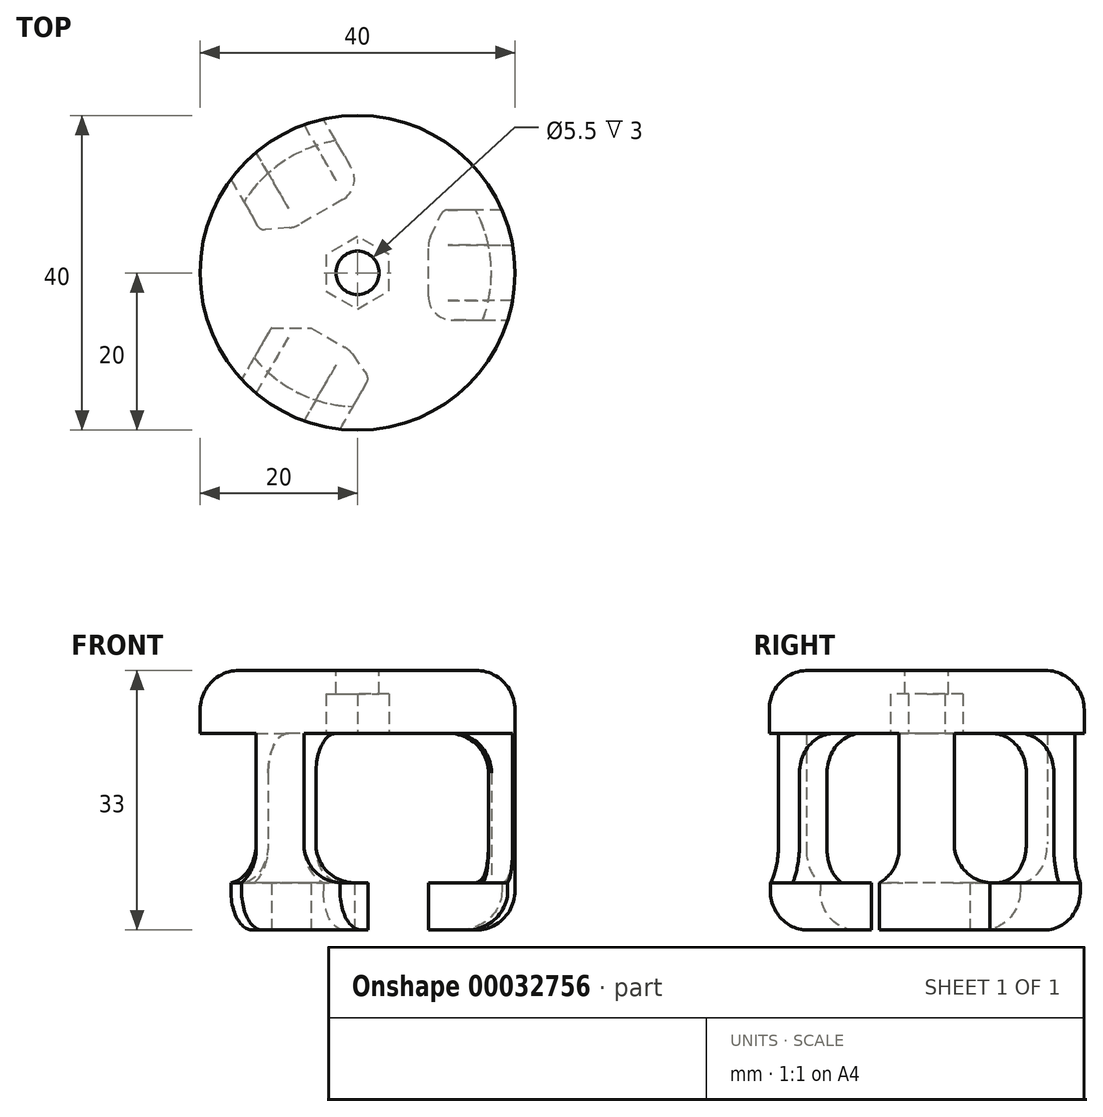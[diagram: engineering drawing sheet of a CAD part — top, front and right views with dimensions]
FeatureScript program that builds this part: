
annotation { "Feature Type Name" : "Feature", "Feature Type Description" : "" }
export const myFeature = defineFeature(function(context is Context, id is Id, definition is map)
    precondition{}
    {
        {
            var Q0;
            Q0=qCreatedBy(makeId("Front.planeOp"),FACE);
            var sketch = newSketch(context, id + "F0", { "sketchPlane" : qUnion([Q0])});
            skLineSegment(sketch, "E0", {"start": v(0, 0) * mm, "end": v(20, 0) * mm});
            skLineSegment(sketch, "E1", {"start": v(20, -33) * mm, "end": v(10, -33) * mm});
            skLineSegment(sketch, "E2", {"start": v(10, -33) * mm, "end": v(10, -28) * mm});
            skLineSegment(sketch, "E3", {"start": v(10, -28) * mm, "end": v(17, -28) * mm});
            skLineSegment(sketch, "E4", {"start": v(0, -8) * mm, "end": v(0, 0) * mm});
            skLineSegment(sketch, "E5", {"start": v(0, 0) * mm, "end": v(0, 12.35) * mm, "construction": true});
            skLineSegment(sketch, "E6", {"start": v(20, 0) * mm, "end": v(20, -33) * mm});
            skLineSegment(sketch, "E7", {"start": v(0, -8) * mm, "end": v(17, -8) * mm});
            skLineSegment(sketch, "E8", {"start": v(17, -8) * mm, "end": v(17, -28) * mm});
            skSolve(sketch);
        }
        {
            var Q0;
            Q0 = qSketchRegion(id + "F0", true);
            var Q1;
            Q1=sQuery(id+"F0.wireOp",EDGE,"E5");
            revolve(context, id + "F1", {"entities" : qUnion([Q0]), "axis" : qUnion([Q1]), "revolveType" : RevolveType.FULL});
        }
        {
            var Q0;
            Q0=makeQuery(id+"F1.opRevolve","SWEPT_FACE",FACE,{"disambiguationData":[OSD([sQuery(id+"F0.wireOp",EDGE,"E1")])]});
            var sketch = newSketch(context, id + "F2", { "sketchPlane" : qUnion([Q0])});
            skLineSegment(sketch, "E9.bottom", {"start": v(7, 0) * mm, "end": v(22.64, 0) * mm});
            skLineSegment(sketch, "E9.top", {"start": v(7, 3) * mm, "end": v(22.64, 3) * mm});
            skLineSegment(sketch, "E9.left", {"start": v(7, 0) * mm, "end": v(7, 3) * mm});
            skLineSegment(sketch, "E9.right", {"start": v(22.64, 0) * mm, "end": v(22.64, 3) * mm});
            skPoint(sketch, "E10", {"position": v(7, 1.5) * mm});
            skLineSegment(sketch, "E11.1.0", {"start": v(-3.5, 6.06) * mm, "end": v(-6.1, 4.56) * mm});
            skLineSegment(sketch, "E11.1.1", {"start": v(-3.5, 6.06) * mm, "end": v(-11.32, 19.6) * mm});
            skLineSegment(sketch, "E11.1.2", {"start": v(-6.1, 4.56) * mm, "end": v(-13.92, 18.1) * mm});
            skLineSegment(sketch, "E11.1.3", {"start": v(-11.32, 19.6) * mm, "end": v(-13.92, 18.1) * mm});
            skPoint(sketch, "E11.1.4", {"position": v(-4.8, 5.31) * mm});
            skLineSegment(sketch, "E11.2.0", {"start": v(-3.5, -6.06) * mm, "end": v(-0.9, -7.56) * mm});
            skLineSegment(sketch, "E11.2.1", {"start": v(-3.5, -6.06) * mm, "end": v(-11.32, -19.6) * mm});
            skLineSegment(sketch, "E11.2.2", {"start": v(-0.9, -7.56) * mm, "end": v(-8.72, -21.1) * mm});
            skLineSegment(sketch, "E11.2.3", {"start": v(-11.32, -19.6) * mm, "end": v(-8.72, -21.1) * mm});
            skPoint(sketch, "E11.2.4", {"position": v(-2.2, -6.81) * mm});
            skPoint(sketch, "E11.center", {"position": v(0, 0) * mm});
            skCircle(sketch, "E12", {"center": v(0, 0) * mm, "radius": 27.07 * mm});
            skSolve(sketch);
        }
        {
            var Q0;
            Q0 = qSketchRegion(id + "F2", true);
            var Q1;
            Q1=makeQuery(id+"F1.opRevolve","SWEPT_FACE",FACE,{"disambiguationData":[OSD([sQuery(id+"F0.wireOp",EDGE,"507b1540-1300-4f00-8e0e-256bcd7e9e75")])]});
            extrude(context, id + "F3", {"entities" : qUnion([Q0]), "operationType" : NewBodyOperationType.REMOVE, "oppositeDirection" : true, "endBoundEntityFace" : qUnion([Q1]), "depth" : 6 * mm});
        }
        {
            var Q0;
            Q0=makeQuery(id+"F1.opRevolve","SWEPT_FACE",FACE,{"disambiguationData":[OSD([sQuery(id+"F0.wireOp",EDGE,"E1")])]});
            var sketch = newSketch(context, id + "F4", { "sketchPlane" : qUnion([Q0])});
            skLineSegment(sketch, "E13", {"start": v(9.28, -4.6) * mm, "end": v(10.6, -7.42) * mm});
            skLineSegment(sketch, "E14", {"start": v(19.08, 6) * mm, "end": v(12, 6) * mm});
            skPoint(sketch, "E15.visualSharp", {"position": v(8.5, 6) * mm});
            skArc(sketch, "E15.filletArc", {"start": v(12, 6) * mm, "mid": v(9.88, 5.12) * mm, "end": v(9, 3) * mm});
            skArc(sketch, "E16.filletArc", {"start": v(10.6, -7.42) * mm, "mid": v(10.97, -7.84) * mm, "end": v(11.5, -8) * mm});
            skArc(sketch, "E17", {"start": v(18.33, -8) * mm, "mid": v(19.97, -1.07) * mm, "end": v(19.08, 6) * mm});
            skLineSegment(sketch, "E18", {"start": v(11.5, -8) * mm, "end": v(18.33, -8) * mm});
            skLineSegment(sketch, "E19", {"start": v(9, 3) * mm, "end": v(9, -3.33) * mm});
            skPoint(sketch, "E20.visualSharp", {"position": v(9, -4) * mm});
            skArc(sketch, "E20.filletArc", {"start": v(9, -3.33) * mm, "mid": v(9.07, -3.98) * mm, "end": v(9.28, -4.6) * mm});
            skLineSegment(sketch, "E21.1.0", {"start": v(-14.74, 13.52) * mm, "end": v(-11.2, 7.4) * mm});
            skPoint(sketch, "E21.1.1", {"position": v(-1.04, 9.8) * mm});
            skPoint(sketch, "E21.1.2", {"position": v(-9.45, 4.36) * mm});
            skArc(sketch, "E21.1.3", {"start": v(-11.2, 7.4) * mm, "mid": v(-9.37, 6) * mm, "end": v(-7.1, 6.3) * mm});
            skLineSegment(sketch, "E21.1.4", {"start": v(-0.65, 10.34) * mm, "end": v(1.13, 12.89) * mm});
            skLineSegment(sketch, "E21.1.5", {"start": v(-7.1, 6.3) * mm, "end": v(-1.61, 9.46) * mm});
            skLineSegment(sketch, "E21.1.6", {"start": v(1.18, 13.96) * mm, "end": v(-2.24, 19.87) * mm});
            skArc(sketch, "E21.1.7", {"start": v(-2.24, 19.87) * mm, "mid": v(-9.06, 17.83) * mm, "end": v(-14.74, 13.52) * mm});
            skArc(sketch, "E21.1.8", {"start": v(1.13, 12.89) * mm, "mid": v(1.31, 13.42) * mm, "end": v(1.18, 13.96) * mm});
            skArc(sketch, "E21.1.9", {"start": v(-1.61, 9.46) * mm, "mid": v(-1.09, 9.85) * mm, "end": v(-0.65, 10.34) * mm});
            skLineSegment(sketch, "E21.2.0", {"start": v(-4.34, -19.52) * mm, "end": v(-0.8, -13.4) * mm});
            skPoint(sketch, "E21.2.1", {"position": v(-7.96, -5.8) * mm});
            skPoint(sketch, "E21.2.2", {"position": v(0.95, -10.36) * mm});
            skArc(sketch, "E21.2.3", {"start": v(-0.8, -13.4) * mm, "mid": v(-0.5, -11.12) * mm, "end": v(-1.9, -9.3) * mm});
            skLineSegment(sketch, "E21.2.4", {"start": v(-8.63, -5.74) * mm, "end": v(-11.73, -5.47) * mm});
            skLineSegment(sketch, "E21.2.5", {"start": v(-1.9, -9.3) * mm, "end": v(-7.39, -6.13) * mm});
            skLineSegment(sketch, "E21.2.6", {"start": v(-12.68, -5.96) * mm, "end": v(-16.1, -11.87) * mm});
            skArc(sketch, "E21.2.7", {"start": v(-16.1, -11.87) * mm, "mid": v(-10.91, -16.76) * mm, "end": v(-4.34, -19.52) * mm});
            skArc(sketch, "E21.2.8", {"start": v(-11.73, -5.47) * mm, "mid": v(-12.28, -5.57) * mm, "end": v(-12.68, -5.96) * mm});
            skArc(sketch, "E21.2.9", {"start": v(-7.39, -6.13) * mm, "mid": v(-7.99, -5.86) * mm, "end": v(-8.63, -5.74) * mm});
            skSolve(sketch);
        }
        {
            var Q0;
            Q0 = qSketchRegion(id + "F4", true);
            var Q1;
            Q1=makeQuery(id+"F3.boolean.opBoolean","COPY",FACE,{"disambiguationData":[OD(0.0)],"derivedFrom":makeQuery(id+"F3.opExtrude","CAP_FACE",FACE,{"disambiguationData":[OSD([sQuery(id+"F2.wireOp",EDGE,"E9.bottom"),sQuery(id+"F2.wireOp",EDGE,"E9.top"),sQuery(id+"F2.wireOp",EDGE,"E9.left"),sQuery(id+"F2.wireOp",EDGE,"E9.right"),sQuery(id+"F2.wireOp",EDGE,"E11.1.0"),sQuery(id+"F2.wireOp",EDGE,"E11.1.1"),sQuery(id+"F2.wireOp",EDGE,"E11.1.2"),sQuery(id+"F2.wireOp",EDGE,"E11.1.3"),sQuery(id+"F2.wireOp",EDGE,"E11.2.0"),sQuery(id+"F2.wireOp",EDGE,"E11.2.1"),sQuery(id+"F2.wireOp",EDGE,"E11.2.2"),sQuery(id+"F2.wireOp",EDGE,"E11.2.3"),sQuery(id+"F2.wireOp",EDGE,"E12")])],"isStart":false})});
            extrude(context, id + "F5", {"entities" : qUnion([Q0]), "operationType" : NewBodyOperationType.ADD, "endBound" : BoundingType.UP_TO_SURFACE, "oppositeDirection" : true, "endBoundEntityFace" : qUnion([Q1]), "depth" : 25 * mm});
        }
        {
            var Q0;
            Q0=makeQuery(id+"F3.boolean.opBoolean","COPY",FACE,{"disambiguationData":[OD(0.0)],"derivedFrom":makeQuery(id+"F3.opExtrude","CAP_FACE",FACE,{"disambiguationData":[OSD([sQuery(id+"F2.wireOp",EDGE,"E9.bottom"),sQuery(id+"F2.wireOp",EDGE,"E9.top"),sQuery(id+"F2.wireOp",EDGE,"E9.left"),sQuery(id+"F2.wireOp",EDGE,"E9.right"),sQuery(id+"F2.wireOp",EDGE,"E11.1.0"),sQuery(id+"F2.wireOp",EDGE,"E11.1.1"),sQuery(id+"F2.wireOp",EDGE,"E11.1.2"),sQuery(id+"F2.wireOp",EDGE,"E11.1.3"),sQuery(id+"F2.wireOp",EDGE,"E11.2.0"),sQuery(id+"F2.wireOp",EDGE,"E11.2.1"),sQuery(id+"F2.wireOp",EDGE,"E11.2.2"),sQuery(id+"F2.wireOp",EDGE,"E11.2.3"),sQuery(id+"F2.wireOp",EDGE,"E12")])],"isStart":false})});
            var sketch = newSketch(context, id + "F6", { "sketchPlane" : qUnion([Q0])});
            skArc(sketch, "E22", {"start": v(16.64, -3.5) * mm, "mid": v(17, 0) * mm, "end": v(16.64, 3.5) * mm, "construction": true});
            skArc(sketch, "E23", {"start": v(21.66, -3.5) * mm, "mid": v(21.94, 0) * mm, "end": v(21.66, 3.5) * mm, "construction": true});
            skLineSegment(sketch, "E24", {"start": v(16.64, 3.5) * mm, "end": v(21.66, 3.5) * mm});
            skLineSegment(sketch, "E25", {"start": v(21.66, -3.5) * mm, "end": v(16.64, -3.5) * mm});
            skArc(sketch, "E26.1.0", {"start": v(-5.29, 16.16) * mm, "mid": v(-8.5, 14.72) * mm, "end": v(-11.35, 12.66) * mm, "construction": true});
            skArc(sketch, "E26.1.1", {"start": v(-7.8, 20.5) * mm, "mid": v(-10.97, 19) * mm, "end": v(-13.86, 17) * mm, "construction": true});
            skLineSegment(sketch, "E26.1.2", {"start": v(-7.8, 20.5) * mm, "end": v(-5.29, 16.16) * mm});
            skLineSegment(sketch, "E26.1.3", {"start": v(-11.35, 12.66) * mm, "end": v(-13.86, 17) * mm});
            skArc(sketch, "E26.2.0", {"start": v(-11.35, -12.66) * mm, "mid": v(-8.5, -14.72) * mm, "end": v(-5.29, -16.16) * mm, "construction": true});
            skArc(sketch, "E26.2.1", {"start": v(-13.86, -17) * mm, "mid": v(-10.97, -19) * mm, "end": v(-7.8, -20.5) * mm, "construction": true});
            skLineSegment(sketch, "E26.2.2", {"start": v(-13.86, -17) * mm, "end": v(-11.35, -12.66) * mm});
            skLineSegment(sketch, "E26.2.3", {"start": v(-5.29, -16.16) * mm, "end": v(-7.8, -20.5) * mm});
            skArc(sketch, "E27", {"start": v(16.64, 3.5) * mm, "mid": v(8.5, 14.72) * mm, "end": v(-5.29, 16.16) * mm});
            skArc(sketch, "E28", {"start": v(-11.35, 12.66) * mm, "mid": v(-17, 0) * mm, "end": v(-11.35, -12.66) * mm});
            skArc(sketch, "E29", {"start": v(-5.29, -16.16) * mm, "mid": v(8.5, -14.72) * mm, "end": v(16.64, -3.5) * mm});
            skArc(sketch, "E30", {"start": v(21.66, 3.5) * mm, "mid": v(10.97, 19) * mm, "end": v(-7.8, 20.5) * mm});
            skArc(sketch, "E31", {"start": v(-13.86, 17) * mm, "mid": v(-21.94, 0) * mm, "end": v(-13.86, -17) * mm});
            skArc(sketch, "E32", {"start": v(-7.8, -20.5) * mm, "mid": v(10.97, -19) * mm, "end": v(21.66, -3.5) * mm});
            skSolve(sketch);
        }
        {
            var Q0;
            Q0 = qSketchRegion(id + "F6", true);
            var Q1;
            Q1=makeQuery(id+"F1.opRevolve","SWEPT_FACE",FACE,{"disambiguationData":[OSD([sQuery(id+"F0.wireOp",EDGE,"E7")])]});
            extrude(context, id + "F7", {"entities" : qUnion([Q0]), "operationType" : NewBodyOperationType.REMOVE, "endBound" : BoundingType.UP_TO_SURFACE, "oppositeDirection" : true, "endBoundEntityFace" : qUnion([Q1]), "depth" : 18 * mm});
        }
        {
            var Q0;
            Q0=makeQuery(id+"FRc7LSiDmBRHnpg_1.opFillet","SPLIT",FACE,{"disambiguationData":[OD(0.0)],"derivedFrom":makeQuery(id+"F1.opRevolve","SWEPT_FACE",FACE,{"disambiguationData":[OSD([sQuery(id+"F0.wireOp",EDGE,"E0")])]})});
            var sketch = newSketch(context, id + "F8", { "sketchPlane" : qUnion([Q0])});
            skLineSegment(sketch, "E33", {"start": v(12.7, 22) * mm, "end": v(0, 0) * mm});
            skPoint(sketch, "E34.endSnap0", {"position": v(-6, 0) * mm});
            skLineSegment(sketch, "E35", {"start": v(0, 0) * mm, "end": v(26.35, 0) * mm});
            skSolve(sketch);
        }
        {
            var Q0;
            Q0=makeQuery(id+"F7.boolean.opBoolean","COPY",EDGE,{"derivedFrom":makeQuery(id+"F7.opExtrude","CAP_EDGE",EDGE,{"disambiguationData":[OSD([sQuery(id+"F6.wireOp",EDGE,"E25")])],"isStart":true})});
            var Q1;
            Q1=makeQuery(id+"F7.boolean.opBoolean","COPY",EDGE,{"derivedFrom":makeQuery(id+"F7.opExtrude","CAP_EDGE",EDGE,{"disambiguationData":[OSD([sQuery(id+"F6.wireOp",EDGE,"E24")])],"isStart":true})});
            var Q2;
            Q2=makeQuery(id+"F7.boolean.opBoolean","COPY",EDGE,{"derivedFrom":makeQuery(id+"F7.opExtrude","CAP_EDGE",EDGE,{"disambiguationData":[OSD([sQuery(id+"F6.wireOp",EDGE,"E26.2.3")])],"isStart":true})});
            var Q3;
            Q3=makeQuery(id+"F7.boolean.opBoolean","COPY",EDGE,{"derivedFrom":makeQuery(id+"F7.opExtrude","CAP_EDGE",EDGE,{"disambiguationData":[OSD([sQuery(id+"F6.wireOp",EDGE,"E26.2.2")])],"isStart":true})});
            var Q4;
            Q4=makeQuery(id+"F7.boolean.opBoolean","COPY",EDGE,{"derivedFrom":makeQuery(id+"F7.opExtrude","CAP_EDGE",EDGE,{"disambiguationData":[OSD([sQuery(id+"F6.wireOp",EDGE,"E26.1.3")])],"isStart":true})});
            var Q5;
            Q5=makeQuery(id+"F7.boolean.opBoolean","COPY",EDGE,{"derivedFrom":makeQuery(id+"F7.opExtrude","CAP_EDGE",EDGE,{"disambiguationData":[OSD([sQuery(id+"F6.wireOp",EDGE,"E26.1.2")])],"isStart":true})});
            fillet(context, id + "F9", {"entities" : qUnion([Q0, Q1, Q2, Q3, Q4, Q5]), "radius" : 5 * mm, "tangentPropagation" : true, "allowEdgeOverflow" : false});
        }
        {
            var Q0;
            {var subQ0=sQuery(id+"F0.wireOp",EDGE,"5JU0XVHw-jdRx-ohpi-ptgh-7lzUt1P3IJOZ");var subQ1=sQuery(id+"F0.wireOp",EDGE,"AD1YDz8e-BfkL-U70Y-Slmf-86ug7eZmjnSb");Q0=makeQuery(id+"F7.boolean.opBoolean","SPLIT",EDGE,{"disambiguationData":[TD([makeQuery(id+"F7.opExtrude","SWEPT_FACE",FACE,{"disambiguationData":[OSD([sQuery(id+"F6.wireOp",EDGE,"E26.2.2")])]})])],"derivedFrom":makeQuery(id+"F1.opRevolve","SWEPT_EDGE",EDGE,{"disambiguationData":[OSD([subQ1,subQ0])]})});}
            var Q1;
            {var subQ0=sQuery(id+"F0.wireOp",EDGE,"5JU0XVHw-jdRx-ohpi-ptgh-7lzUt1P3IJOZ");var subQ1=sQuery(id+"F0.wireOp",EDGE,"AD1YDz8e-BfkL-U70Y-Slmf-86ug7eZmjnSb");Q1=makeQuery(id+"F7.boolean.opBoolean","SPLIT",EDGE,{"disambiguationData":[TD([makeQuery(id+"F7.opExtrude","SWEPT_FACE",FACE,{"disambiguationData":[OSD([sQuery(id+"F6.wireOp",EDGE,"E26.1.2")])]})])],"derivedFrom":makeQuery(id+"F1.opRevolve","SWEPT_EDGE",EDGE,{"disambiguationData":[OSD([subQ1,subQ0])]})});}
            var Q2;
            {var subQ0=sQuery(id+"F0.wireOp",EDGE,"5JU0XVHw-jdRx-ohpi-ptgh-7lzUt1P3IJOZ");var subQ1=sQuery(id+"F0.wireOp",EDGE,"AD1YDz8e-BfkL-U70Y-Slmf-86ug7eZmjnSb");Q2=makeQuery(id+"F7.boolean.opBoolean","SPLIT",EDGE,{"disambiguationData":[TD([makeQuery(id+"F7.opExtrude","SWEPT_FACE",FACE,{"disambiguationData":[OSD([sQuery(id+"F6.wireOp",EDGE,"E24")])]})])],"derivedFrom":makeQuery(id+"F1.opRevolve","SWEPT_EDGE",EDGE,{"disambiguationData":[OSD([subQ1,subQ0])]})});}
            var Q3;
            {var subQ0=sQuery(id+"F0.wireOp",EDGE,"E6");var subQ1=sQuery(id+"F0.wireOp",EDGE,"YB5l314j-i3Ki-3XtK-FZlX-X9e5m8dVZ1rk");Q3=makeQuery(id+"F7.boolean.opBoolean","SPLIT",EDGE,{"disambiguationData":[TD([makeQuery(id+"F7.opExtrude","SWEPT_FACE",FACE,{"disambiguationData":[OSD([sQuery(id+"F6.wireOp",EDGE,"E24")])]})])],"derivedFrom":makeQuery(id+"F1.opRevolve","SWEPT_EDGE",EDGE,{"disambiguationData":[OSD([subQ0,subQ1])]})});}
            var Q4;
            {var subQ0=sQuery(id+"F0.wireOp",EDGE,"E6");var subQ1=sQuery(id+"F0.wireOp",EDGE,"YB5l314j-i3Ki-3XtK-FZlX-X9e5m8dVZ1rk");Q4=makeQuery(id+"F7.boolean.opBoolean","SPLIT",EDGE,{"disambiguationData":[TD([makeQuery(id+"F7.opExtrude","SWEPT_FACE",FACE,{"disambiguationData":[OSD([sQuery(id+"F6.wireOp",EDGE,"E26.2.2")])]})])],"derivedFrom":makeQuery(id+"F1.opRevolve","SWEPT_EDGE",EDGE,{"disambiguationData":[OSD([subQ0,subQ1])]})});}
            var Q5;
            {var subQ0=sQuery(id+"F0.wireOp",EDGE,"E6");var subQ1=sQuery(id+"F0.wireOp",EDGE,"YB5l314j-i3Ki-3XtK-FZlX-X9e5m8dVZ1rk");Q5=makeQuery(id+"F7.boolean.opBoolean","SPLIT",EDGE,{"disambiguationData":[TD([makeQuery(id+"F7.opExtrude","SWEPT_FACE",FACE,{"disambiguationData":[OSD([sQuery(id+"F6.wireOp",EDGE,"E26.1.2")])]})])],"derivedFrom":makeQuery(id+"F1.opRevolve","SWEPT_EDGE",EDGE,{"disambiguationData":[OSD([subQ0,subQ1])]})});}
            fillet(context, id + "F10", {"entities" : qUnion([Q0, Q1, Q2, Q3, Q4, Q5]), "radius" : 5 * mm, "tangentPropagation" : true, "allowEdgeOverflow" : false});
        }
        {
            var Q0;
            {var subQ0=sQuery(id+"F0.wireOp",EDGE,"E7");Q0=makeQuery(id+"F7.boolean.opBoolean","MERGE",FACE,{"derivedFrom":[makeQuery(id+"F1.opRevolve","SWEPT_FACE",FACE,{"disambiguationData":[OSD([subQ0])]}),makeQuery(id+"F7.opExtrude","CAP_FACE",FACE,{"disambiguationData":[OSD([subQ0]),ownerDisambiguation([makeQuery(id+"F7.opExtrude","SWEPT_BODY",BODY,{"disambiguationData":[OSD([sQuery(id+"F6.wireOp",EDGE,"E24"),sQuery(id+"F6.wireOp",EDGE,"E26.1.2"),sQuery(id+"F6.wireOp",EDGE,"E27"),sQuery(id+"F6.wireOp",EDGE,"E30")])]})])],"isStart":false}),makeQuery(id+"F7.opExtrude","CAP_FACE",FACE,{"disambiguationData":[OSD([subQ0]),ownerDisambiguation([makeQuery(id+"F7.opExtrude","SWEPT_BODY",BODY,{"disambiguationData":[OSD([sQuery(id+"F6.wireOp",EDGE,"E25"),sQuery(id+"F6.wireOp",EDGE,"E26.2.3"),sQuery(id+"F6.wireOp",EDGE,"E29"),sQuery(id+"F6.wireOp",EDGE,"E32")])]})])],"isStart":false}),makeQuery(id+"F7.opExtrude","CAP_FACE",FACE,{"disambiguationData":[OSD([subQ0]),ownerDisambiguation([makeQuery(id+"F7.opExtrude","SWEPT_BODY",BODY,{"disambiguationData":[OSD([sQuery(id+"F6.wireOp",EDGE,"E26.1.3"),sQuery(id+"F6.wireOp",EDGE,"E26.2.2"),sQuery(id+"F6.wireOp",EDGE,"E28"),sQuery(id+"F6.wireOp",EDGE,"E31")])]})])],"isStart":false})]});}
            var sketch = newSketch(context, id + "F11", { "sketchPlane" : qUnion([Q0])});
            skCircle(sketch, "E36.cCircle", {"center": v(0, 0) * mm, "radius": 4 * mm, "construction": true});
            skLineSegment(sketch, "E36.0", {"start": v(-4, 2.3) * mm, "end": v(0, 4.62) * mm});
            skLineSegment(sketch, "E36.1", {"start": v(0, 4.62) * mm, "end": v(4, 2.3) * mm});
            skLineSegment(sketch, "E36.2", {"start": v(4, 2.3) * mm, "end": v(4, -2.3) * mm});
            skLineSegment(sketch, "E36.3", {"start": v(4, -2.3) * mm, "end": v(0, -4.62) * mm});
            skLineSegment(sketch, "E36.4", {"start": v(0, -4.62) * mm, "end": v(-4, -2.3) * mm});
            skLineSegment(sketch, "E36.5", {"start": v(-4, -2.3) * mm, "end": v(-4, 2.3) * mm});
            skPoint(sketch, "E36.0.midPoint", {"position": v(-2, 3.46) * mm});
            skSolve(sketch);
        }
        {
            var Q0;
            Q0 = qSketchRegion(id + "F11", true);
            extrude(context, id + "F12", {"entities" : qUnion([Q0]), "operationType" : NewBodyOperationType.REMOVE, "oppositeDirection" : true, "depth" : 5 * mm});
        }
        {
            var Q0;
            Q0=sQuery(id+"F8.wireOp",VERTEX,"E35.start");
            var Q1;
            Q1=makeQuery(id+"F1.opRevolve","SWEPT_BODY",BODY,{"disambiguationData":[OSD([sQuery(id+"F0.wireOp",EDGE,"E0"),sQuery(id+"F0.wireOp",EDGE,"E1"),sQuery(id+"F0.wireOp",EDGE,"E2"),sQuery(id+"F0.wireOp",EDGE,"E3"),sQuery(id+"F0.wireOp",EDGE,"E4"),sQuery(id+"F0.wireOp",EDGE,"E6"),sQuery(id+"F0.wireOp",EDGE,"E7"),sQuery(id+"F0.wireOp",EDGE,"oZZgMhXo-IGQ9-ketN-pIXG-lvkoXyTYYKlg"),sQuery(id+"F0.wireOp",EDGE,"dHxaSU61-WMZi-X72z-Avvv-rAPENNYPcqco"),sQuery(id+"F0.wireOp",EDGE,"AD1YDz8e-BfkL-U70Y-Slmf-86ug7eZmjnSb"),sQuery(id+"F0.wireOp",EDGE,"5JU0XVHw-jdRx-ohpi-ptgh-7lzUt1P3IJOZ")])]});
            hole(context, id + "F13", {"style" : HoleStyle.SIMPLE, "endStyle" : HoleEndStyle.THROUGH, "holeDiameter" : 5.5 * mm, "locations" : qUnion([Q0]), "scope" : qUnion([Q1]), "isTappedThrough" : true});
        }
        {
            var Q0;
            Q0=qCreatedBy(makeId("Front.planeOp"),FACE);
            var sketch = newSketch(context, id + "F14", { "sketchPlane" : qUnion([Q0])});
            skLineSegment(sketch, "E37.bottom", {"start": v(-23.38, -22.81) * mm, "end": v(4.84, -22.81) * mm});
            skLineSegment(sketch, "E37.top", {"start": v(-23.38, -36.77) * mm, "end": v(4.84, -36.77) * mm});
            skLineSegment(sketch, "E37.left", {"start": v(-23.38, -22.81) * mm, "end": v(-23.38, -36.77) * mm});
            skLineSegment(sketch, "E37.right", {"start": v(4.84, -22.81) * mm, "end": v(4.84, -36.77) * mm});
            skSolve(sketch);
        }
        {
            var Q0;
            Q0 = qSketchRegion(id + "F14", true);
            extrude(context, id + "F15", {"entities" : qUnion([Q0]), "operationType" : NewBodyOperationType.REMOVE, "depth" : 7 * mm});
        }
        {
            var Q0;
            Q0=qCreatedBy(makeId("Front.planeOp"),FACE);
            cPlane(context, id + "F16", {"entities" : qUnion([Q0]), "cplaneType" : CPlaneType.OFFSET, "offset" : 25 * mm, "oppositeDirection" : true, "width" : 150 * mm, "height" : 150 * mm});
        }
        {
            var Q0;
            {var subQ0=sQuery(id+"F6.wireOp",EDGE,"E24");var subQ1=sQuery(id+"F0.wireOp",EDGE,"E8");var subQ3=sQuery(id+"F0.wireOp",EDGE,"E7");Q0=makeQuery(id+"F7.boolean.opBoolean","SPLIT",EDGE,{"disambiguationData":[TD([makeQuery(id+"F7.opExtrude","SWEPT_FACE",FACE,{"disambiguationData":[OSD([subQ0])]})])],"derivedFrom":makeQuery(id+"F1.opRevolve","SWEPT_EDGE",EDGE,{"disambiguationData":[OSD([subQ3,subQ1])]})});}
            var Q1;
            Q1=makeQuery(id+"F7.boolean.opBoolean","COPY",EDGE,{"derivedFrom":makeQuery(id+"F7.opExtrude","TWEAK_EDGE",EDGE,{"derivedFrom":[makeQuery(id+"F1.opRevolve","SWEPT_FACE",FACE,{"disambiguationData":[OSD([sQuery(id+"F0.wireOp",EDGE,"E7")])]}),makeQuery(id+"F6.imprint","IMPRINT",EDGE,{"derivedFrom":sQuery(id+"F6.wireOp",EDGE,"E25")})]})});
            var Q2;
            Q2=makeQuery(id+"F7.boolean.opBoolean","COPY",EDGE,{"derivedFrom":makeQuery(id+"F7.opExtrude","TWEAK_EDGE",EDGE,{"derivedFrom":[makeQuery(id+"F1.opRevolve","SWEPT_FACE",FACE,{"disambiguationData":[OSD([sQuery(id+"F0.wireOp",EDGE,"E7")])]}),makeQuery(id+"F6.imprint","IMPRINT",EDGE,{"derivedFrom":sQuery(id+"F6.wireOp",EDGE,"E24")})]})});
            var Q3;
            {var subQ0=sQuery(id+"F0.wireOp",EDGE,"E8");var subQ2=sQuery(id+"F6.wireOp",EDGE,"E26.2.2");var subQ3=sQuery(id+"F0.wireOp",EDGE,"E7");Q3=makeQuery(id+"F7.boolean.opBoolean","SPLIT",EDGE,{"disambiguationData":[TD([makeQuery(id+"F7.opExtrude","SWEPT_FACE",FACE,{"disambiguationData":[OSD([subQ2])]})])],"derivedFrom":makeQuery(id+"F1.opRevolve","SWEPT_EDGE",EDGE,{"disambiguationData":[OSD([subQ3,subQ0])]})});}
            var Q4;
            Q4=makeQuery(id+"F7.boolean.opBoolean","COPY",EDGE,{"derivedFrom":makeQuery(id+"F7.opExtrude","TWEAK_EDGE",EDGE,{"derivedFrom":[makeQuery(id+"F1.opRevolve","SWEPT_FACE",FACE,{"disambiguationData":[OSD([sQuery(id+"F0.wireOp",EDGE,"E7")])]}),makeQuery(id+"F6.imprint","IMPRINT",EDGE,{"derivedFrom":sQuery(id+"F6.wireOp",EDGE,"E26.2.3")})]})});
            var Q5;
            Q5=makeQuery(id+"F7.boolean.opBoolean","COPY",EDGE,{"derivedFrom":makeQuery(id+"F7.opExtrude","TWEAK_EDGE",EDGE,{"derivedFrom":[makeQuery(id+"F1.opRevolve","SWEPT_FACE",FACE,{"disambiguationData":[OSD([sQuery(id+"F0.wireOp",EDGE,"E7")])]}),makeQuery(id+"F6.imprint","IMPRINT",EDGE,{"derivedFrom":sQuery(id+"F6.wireOp",EDGE,"E26.2.2")})]})});
            var Q6;
            Q6=makeQuery(id+"F7.boolean.opBoolean","COPY",EDGE,{"derivedFrom":makeQuery(id+"F7.opExtrude","TWEAK_EDGE",EDGE,{"derivedFrom":[makeQuery(id+"F1.opRevolve","SWEPT_FACE",FACE,{"disambiguationData":[OSD([sQuery(id+"F0.wireOp",EDGE,"E7")])]}),makeQuery(id+"F6.imprint","IMPRINT",EDGE,{"derivedFrom":sQuery(id+"F6.wireOp",EDGE,"E26.1.3")})]})});
            var Q7;
            {var subQ1=sQuery(id+"F0.wireOp",EDGE,"E7");var subQ2=sQuery(id+"F6.wireOp",EDGE,"E26.1.2");var subQ3=sQuery(id+"F0.wireOp",EDGE,"E8");Q7=makeQuery(id+"F7.boolean.opBoolean","SPLIT",EDGE,{"disambiguationData":[TD([makeQuery(id+"F7.opExtrude","SWEPT_FACE",FACE,{"disambiguationData":[OSD([subQ2])]})])],"derivedFrom":makeQuery(id+"F1.opRevolve","SWEPT_EDGE",EDGE,{"disambiguationData":[OSD([subQ1,subQ3])]})});}
            var Q8;
            Q8=makeQuery(id+"F7.boolean.opBoolean","COPY",EDGE,{"derivedFrom":makeQuery(id+"F7.opExtrude","TWEAK_EDGE",EDGE,{"derivedFrom":[makeQuery(id+"F1.opRevolve","SWEPT_FACE",FACE,{"disambiguationData":[OSD([sQuery(id+"F0.wireOp",EDGE,"E7")])]}),makeQuery(id+"F6.imprint","IMPRINT",EDGE,{"derivedFrom":sQuery(id+"F6.wireOp",EDGE,"E26.1.2")})]})});
            fillet(context, id + "F17", {"entities" : qUnion([Q0, Q1, Q2, Q3, Q4, Q5, Q6, Q7, Q8]), "radius" : 5 * mm, "tangentPropagation" : true, "allowEdgeOverflow" : false});
        }
    });
